# Revit family: Ladder_Vertical_KattsafeUSA_Caged_GrabRail
name_source: partatom
category: Specialty Equipment
units: mm (PartAtom-declared; Revit-internal decimal feet)

## family parameters
Always vertical = Yes
Classification Number = 23.17.23.15
Cut with Voids When Loaded = No
Enable Cutting in Views = No
Maintain Annotation Orientation = No
Part Type = Normal
Room Calculation Point = No
Round Connector Dimension = Use Diameter
Shared = No
Work Plane-Based = No

## types (1)
- RL41
    Angle = 90.00°
    Assembly Code = E1090100
    Default Elevation = 0' - 0"
    Description = The versatile RL41 model with grab rails improves climbing comfort and confidence. Grab rails mount at the ladder’s head, and another rail bolts at the top to ensure more safety when exiting the ladder. Cut this unit to the exact size and assemble it on-site for a perfect fit.
    ElementType = Ladder
    Export Type to IFC As = IfcBuildingElementProxy
    IfcExportAs = IfcBuildingElementProxy
    IfcExportType = USERDEFINED
    Manufacturer = Kattsafe®
    ManufacturerOverallWidth = 3' - 0 1/2"
    ManufacturerSpecCode = RL41
    ManufacturerURLProductSpecific = https://kattsafe.com
    Material = Aluminum_Kattsafe_Satin
    Model = RL41
    ModifiedIssue = 20250822 $
    Type Comments = Ladder - Caged - Grab Rail
    Type IFC Predefined Type = USERDEFINED
    URL = https://kattsafe.com
    Uniclass2015Code = Pr_25_30_85_02
    Uniclass2015Title = Access ladders
    Uniclass2015Version = Products v1.35

## geometry (parser evidence)
native form markers: Sweep x13
no freeform markers — native parametric forms only
